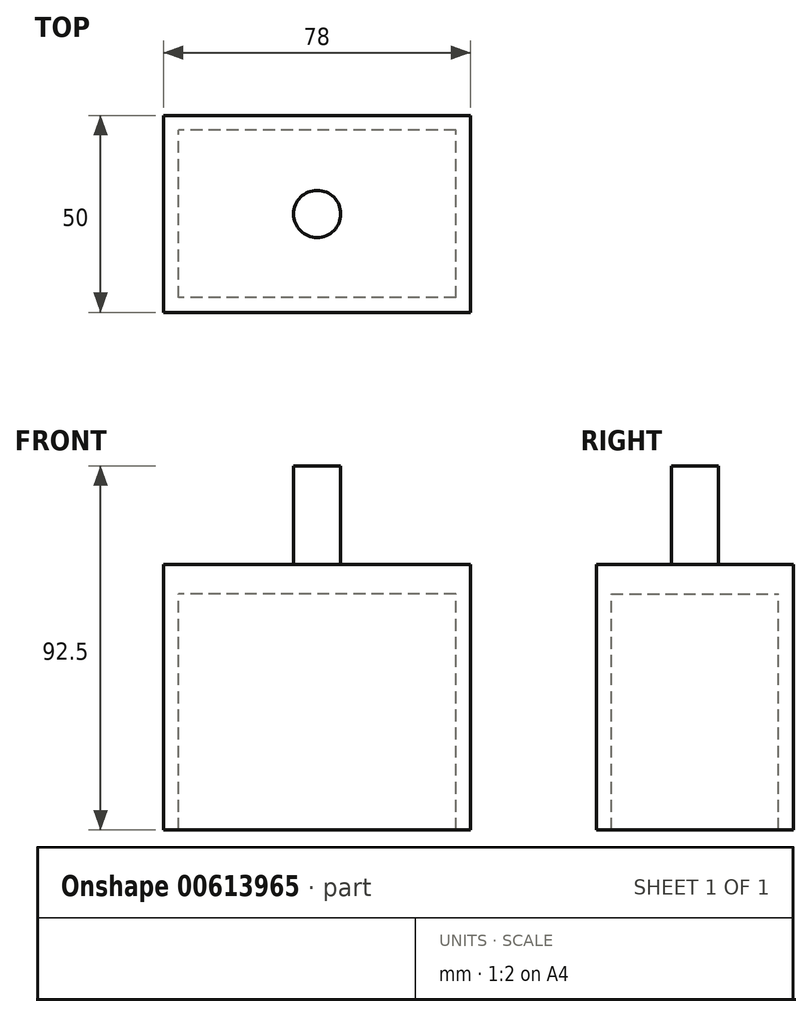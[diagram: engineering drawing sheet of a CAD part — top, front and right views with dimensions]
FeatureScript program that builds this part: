
annotation { "Feature Type Name" : "Feature", "Feature Type Description" : "" }
export const myFeature = defineFeature(function(context is Context, id is Id, definition is map)
    precondition{}
    {
        {
            var Q0;
            Q0=qCreatedBy(makeId("Top.planeOp"),FACE);
            var sketch = newSketch(context, id + "F0", { "sketchPlane" : qUnion([Q0])});
            skLineSegment(sketch, "E0.bottom", {"start": v(39, -25) * mm, "end": v(-39, -25) * mm});
            skLineSegment(sketch, "E0.top", {"start": v(39, 25) * mm, "end": v(-39, 25) * mm});
            skLineSegment(sketch, "E0.left", {"start": v(39, -25) * mm, "end": v(39, 25) * mm});
            skLineSegment(sketch, "E0.right", {"start": v(-39, -25) * mm, "end": v(-39, 25) * mm});
            skPoint(sketch, "E0.middle", {"position": v(0, 0) * mm});
            skSolve(sketch);
        }
        {
            var Q0;
            Q0 = qSketchRegion(id + "F0", true);
            extrude(context, id + "F1", {"entities" : qUnion([Q0]), "depth" : 7.5 * mm, "offsetDistance" : 25.4 * mm});
        }
        {
            var Q0;
            Q0=makeQuery(id+"F1.opExtrude","CAP_FACE",FACE,{"disambiguationData":[OSD([sQuery(id+"F0.wireOp",EDGE,"E0.bottom"),sQuery(id+"F0.wireOp",EDGE,"E0.top"),sQuery(id+"F0.wireOp",EDGE,"E0.left"),sQuery(id+"F0.wireOp",EDGE,"E0.right")])],"isStart":false});
            var sketch = newSketch(context, id + "F2", { "sketchPlane" : qUnion([Q0])});
            skLineSegment(sketch, "E1", {"start": v(-39, 0) * mm, "end": v(39, 0) * mm});
            skLineSegment(sketch, "E2", {"start": v(0, 0) * mm, "end": v(-39, 0) * mm});
            skCircle(sketch, "E3", {"center": v(0, 0) * mm, "radius": 6 * mm});
            skCircle(sketch, "E4", {"center": v(-18.85, -0.43) * mm, "radius": 6 * mm});
            skLineSegment(sketch, "E5", {"start": v(0, 0) * mm, "end": v(39, 0) * mm});
            skCircle(sketch, "E6", {"center": v(19.13, -0.3) * mm, "radius": 6 * mm});
            skSolve(sketch);
        }
        {
            var Q0;
            {var subQ0=sQuery(id+"F2.wireOp",EDGE,"E4");var subQ1=sQuery(id+"F2.wireOp",EDGE,"E2");var subQ2=makeQuery(id+"F2.imprint","INTERSECT",VERTEX,{"disambiguationData":[OD(0.0)],"derivedFrom":[subQ1,subQ0]});Q0=makeQuery(id+"F2.imprint","IMPRINT",FACE,{"disambiguationData":[TD([[makeQuery(id+"F2.imprint","IMPRINT",EDGE,{"disambiguationData":[TD([[subQ2,-1.0]])],"derivedFrom":subQ1}),1.0]])]});}
            var Q1;
            {var subQ0=sQuery(id+"F2.wireOp",EDGE,"E4");var subQ1=sQuery(id+"F2.wireOp",EDGE,"E2");var subQ2=makeQuery(id+"F2.imprint","INTERSECT",VERTEX,{"disambiguationData":[OD(0.0)],"derivedFrom":[subQ1,subQ0]});Q1=makeQuery(id+"F2.imprint","IMPRINT",FACE,{"disambiguationData":[TD([[makeQuery(id+"F2.imprint","IMPRINT",EDGE,{"disambiguationData":[TD([[subQ2,-1.0]])],"derivedFrom":subQ1}),-1.0]])]});}
            var Q2;
            {var subQ0=sQuery(id+"F2.wireOp",EDGE,"E2");var subQ1=sQuery(id+"F2.wireOp",EDGE,"E3");var subQ2=makeQuery(id+"F2.imprint","INTERSECT",VERTEX,{"derivedFrom":[subQ1,subQ0]});Q2=makeQuery(id+"F2.imprint","IMPRINT",FACE,{"disambiguationData":[TD([[makeQuery(id+"F2.imprint","IMPRINT",EDGE,{"disambiguationData":[TD([[subQ2,1.0]])],"derivedFrom":subQ1}),1.0]])]});}
            var Q3;
            {var subQ0=sQuery(id+"F2.wireOp",EDGE,"E2");var subQ1=sQuery(id+"F2.wireOp",EDGE,"E3");var subQ2=makeQuery(id+"F2.imprint","INTERSECT",VERTEX,{"derivedFrom":[subQ1,subQ0]});Q3=makeQuery(id+"F2.imprint","IMPRINT",FACE,{"disambiguationData":[TD([[makeQuery(id+"F2.imprint","IMPRINT",EDGE,{"disambiguationData":[TD([[subQ2,-1.0]])],"derivedFrom":subQ1}),1.0]])]});}
            var Q4;
            {var subQ0=sQuery(id+"F2.wireOp",EDGE,"E6");var subQ1=sQuery(id+"F2.wireOp",EDGE,"E5");var subQ2=makeQuery(id+"F2.imprint","INTERSECT",VERTEX,{"disambiguationData":[OD(0.0)],"derivedFrom":[subQ1,subQ0]});Q4=makeQuery(id+"F2.imprint","IMPRINT",FACE,{"disambiguationData":[TD([[makeQuery(id+"F2.imprint","IMPRINT",EDGE,{"disambiguationData":[TD([[subQ2,-1.0]])],"derivedFrom":subQ1}),1.0]])]});}
            var Q5;
            {var subQ0=sQuery(id+"F2.wireOp",EDGE,"E6");var subQ1=sQuery(id+"F2.wireOp",EDGE,"E5");var subQ2=makeQuery(id+"F2.imprint","INTERSECT",VERTEX,{"disambiguationData":[OD(0.0)],"derivedFrom":[subQ1,subQ0]});Q5=makeQuery(id+"F2.imprint","IMPRINT",FACE,{"disambiguationData":[TD([[makeQuery(id+"F2.imprint","IMPRINT",EDGE,{"disambiguationData":[TD([[subQ2,-1.0]])],"derivedFrom":subQ1}),-1.0]])]});}
            extrude(context, id + "F3", {"entities" : qUnion([Q0, Q1, Q2, Q3, Q4, Q5]), "operationType" : NewBodyOperationType.ADD, "depth" : 25 * mm, "offsetDistance" : 25.4 * mm});
        }
        {
            var Q0;
            Q0=makeQuery(id+"F1.opExtrude","CAP_FACE",FACE,{"disambiguationData":[OSD([sQuery(id+"F0.wireOp",EDGE,"E0.bottom"),sQuery(id+"F0.wireOp",EDGE,"E0.top"),sQuery(id+"F0.wireOp",EDGE,"E0.left"),sQuery(id+"F0.wireOp",EDGE,"E0.right")])],"isStart":true});
            var sketch = newSketch(context, id + "F4", { "sketchPlane" : qUnion([Q0])});
            skLineSegment(sketch, "E7.bottom", {"start": v(35.25, 21.25) * mm, "end": v(-35.25, 21.25) * mm});
            skLineSegment(sketch, "E7.top", {"start": v(35.25, -21.25) * mm, "end": v(-35.25, -21.25) * mm});
            skLineSegment(sketch, "E7.left", {"start": v(35.25, 21.25) * mm, "end": v(35.25, -21.25) * mm});
            skLineSegment(sketch, "E7.right", {"start": v(-35.25, 21.25) * mm, "end": v(-35.25, -21.25) * mm});
            skPoint(sketch, "E7.middle", {"position": v(0, 0) * mm});
            skSolve(sketch);
        }
        {
            var Q0;
            Q0=makeQuery(id+"F4.imprint","IMPRINT",FACE,{"disambiguationData":[TD([[makeQuery(id+"F4.imprint","IMPRINT",EDGE,{"derivedFrom":sQuery(id+"F4.wireOp",EDGE,"E7.bottom")}),-1.0]])]});
            extrude(context, id + "F5", {"entities" : qUnion([Q0]), "operationType" : NewBodyOperationType.ADD, "depth" : 60 * mm, "offsetDistance" : 25.4 * mm});
        }
    });
